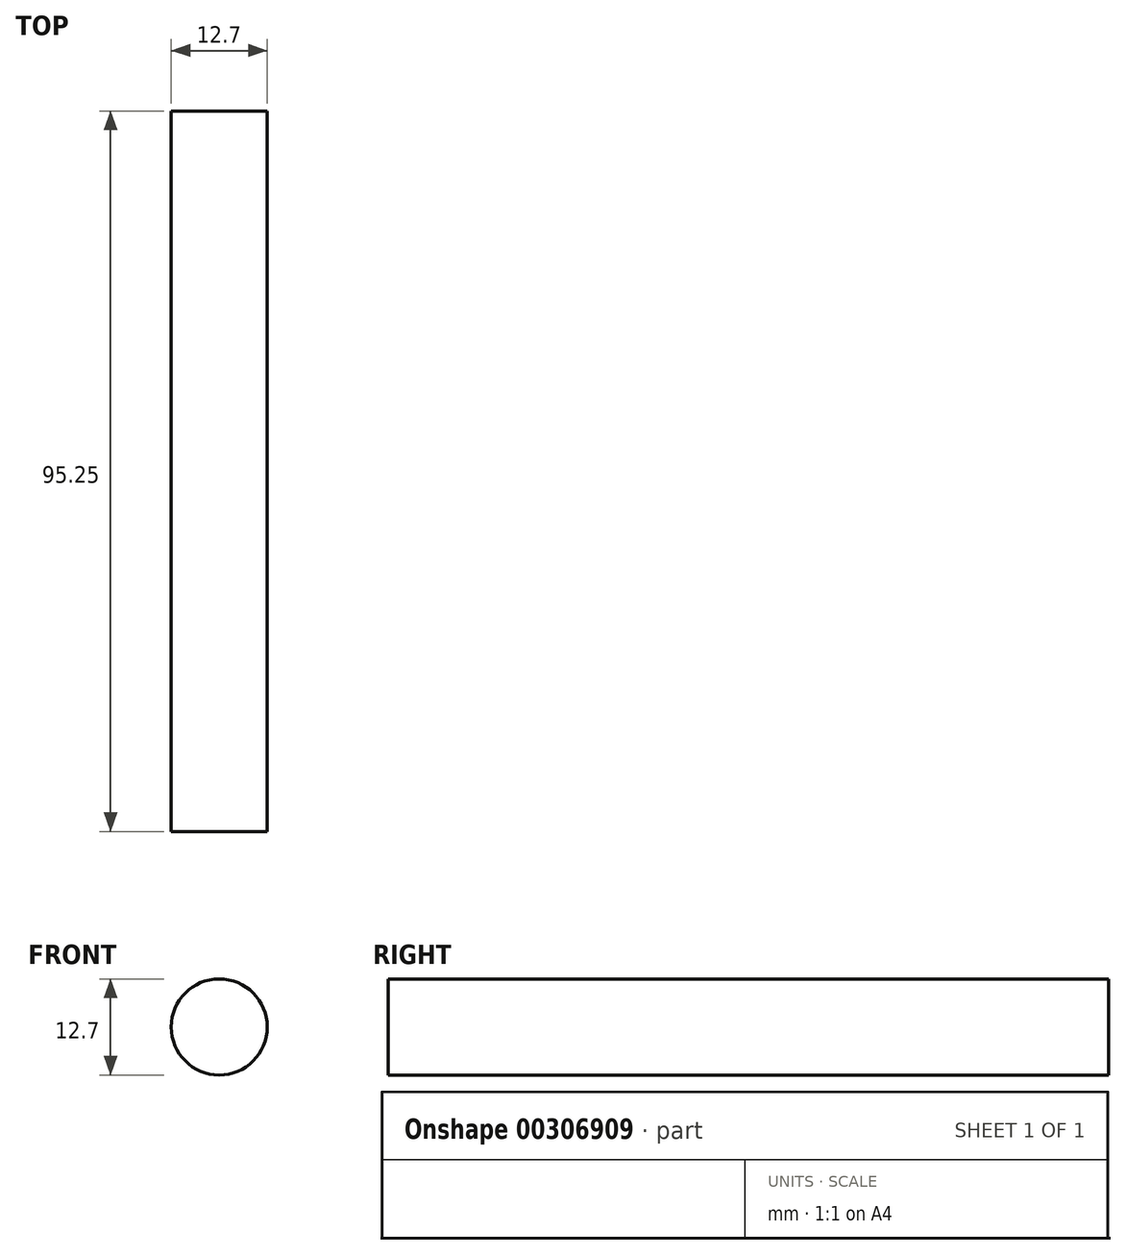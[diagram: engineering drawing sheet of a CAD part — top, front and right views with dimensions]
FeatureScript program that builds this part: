
annotation { "Feature Type Name" : "Feature", "Feature Type Description" : "" }
export const myFeature = defineFeature(function(context is Context, id is Id, definition is map)
    precondition{}
    {
        {
            var Q0;
            Q0=qCreatedBy(makeId("Front.planeOp"),FACE);
            var sketch = newSketch(context, id + "F0", { "sketchPlane" : qUnion([Q0])});
            skCircle(sketch, "E0", {"center": v(0, 0) * mm, "radius": 6.35 * mm});
            skSolve(sketch);
        }
        {
            var Q0;
            Q0 = qSketchRegion(id + "F0", true);
            extrude(context, id + "F1", {"entities" : qUnion([Q0]), "depth" : 95.25 * mm});
        }
    });
